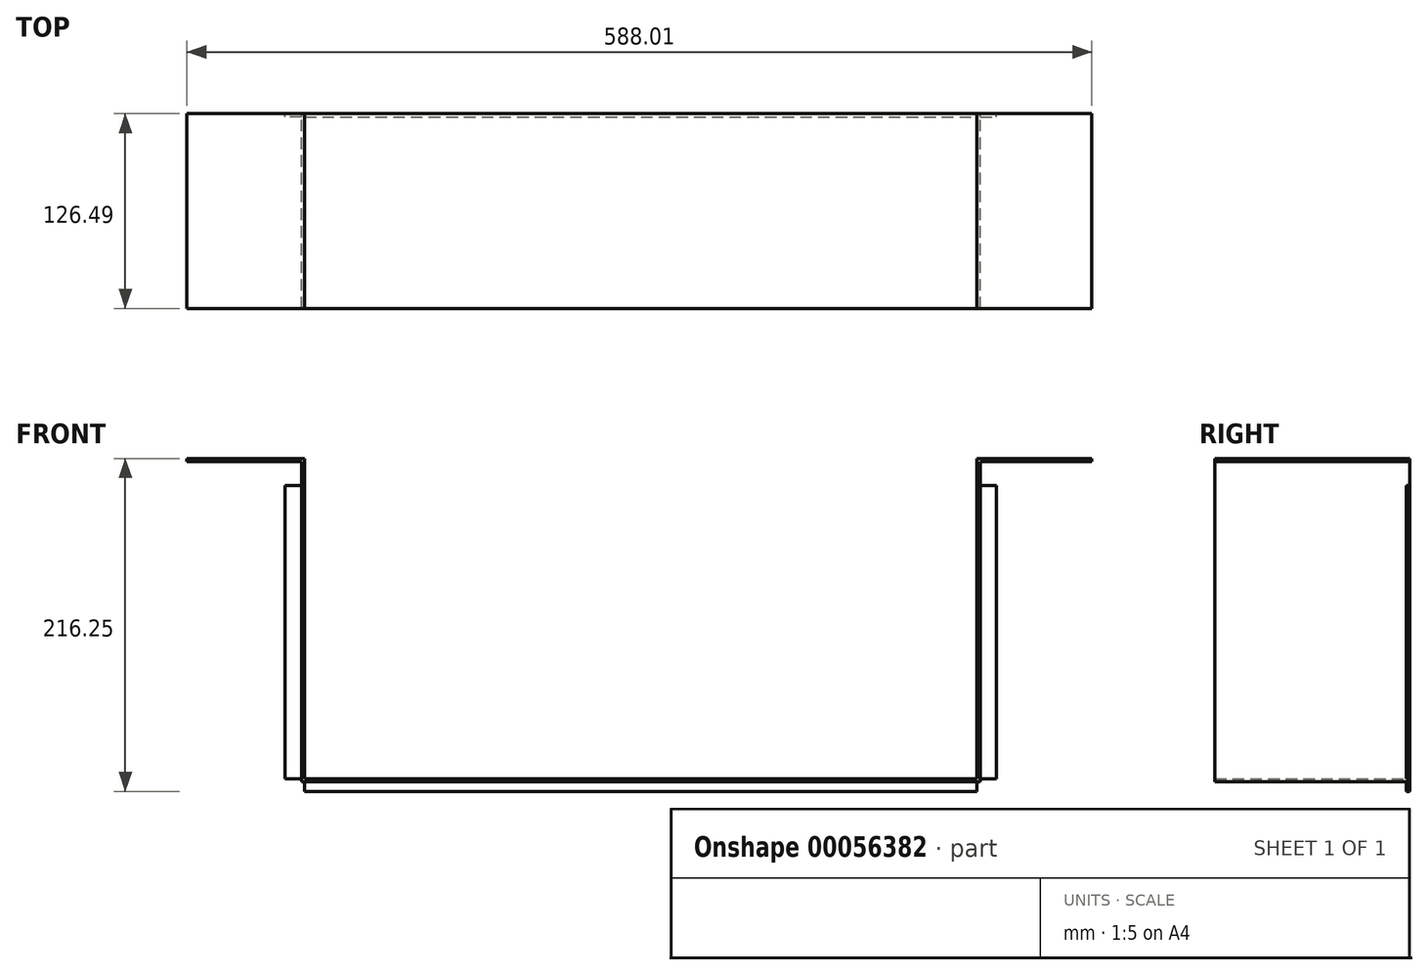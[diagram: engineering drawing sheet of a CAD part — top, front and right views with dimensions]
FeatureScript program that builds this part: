
annotation { "Feature Type Name" : "Feature", "Feature Type Description" : "" }
export const myFeature = defineFeature(function(context is Context, id is Id, definition is map)
    precondition{}
    {
        {
            var Q0;
            Q0=qCreatedBy(makeId("Front.planeOp"),FACE);
            var sketch = newSketch(context, id + "F0", { "sketchPlane" : qUnion([Q0])});
            skLineSegment(sketch, "E0", {"start": v(0, 0) * mm, "end": v(436.88, 0) * mm});
            skLineSegment(sketch, "E1", {"start": v(438.91, 0) * mm, "end": v(438.91, 206.04) * mm});
            skLineSegment(sketch, "E2", {"start": v(438.91, 206.04) * mm, "end": v(511.43, 206.04) * mm});
            skLineSegment(sketch, "E3", {"start": v(0, 0) * mm, "end": v(0, 206.04) * mm});
            skLineSegment(sketch, "E4", {"start": v(-2.03, 206.04) * mm, "end": v(-76.58, 206.04) * mm});
            skLineSegment(sketch, "E5", {"start": v(-76.58, 206.04) * mm, "end": v(-76.58, 208.08) * mm});
            skLineSegment(sketch, "E6", {"start": v(-76.58, 208.08) * mm, "end": v(-2.03, 208.08) * mm});
            skLineSegment(sketch, "E7", {"start": v(-2.03, 206.04) * mm, "end": v(-2.03, 0) * mm});
            skLineSegment(sketch, "E8", {"start": v(-2.03, -2.03) * mm, "end": v(436.88, -2.03) * mm});
            skLineSegment(sketch, "E9", {"start": v(436.88, 0) * mm, "end": v(436.88, 208.08) * mm});
            skLineSegment(sketch, "E10", {"start": v(436.88, 208.08) * mm, "end": v(511.43, 208.08) * mm});
            skLineSegment(sketch, "E11", {"start": v(511.43, 208.08) * mm, "end": v(511.43, 206.04) * mm});
            skLineSegment(sketch, "E12", {"start": v(0, -2.03) * mm, "end": v(-2.03, -2.03) * mm});
            skLineSegment(sketch, "E13", {"start": v(436.88, -2.03) * mm, "end": v(438.91, -2.03) * mm});
            skLineSegment(sketch, "E14", {"start": v(438.91, -2.03) * mm, "end": v(438.91, 0) * mm});
            skLineSegment(sketch, "E15", {"start": v(-2.03, 208.08) * mm, "end": v(0, 208.08) * mm});
            skLineSegment(sketch, "E16", {"start": v(0, 208.08) * mm, "end": v(0, 206.04) * mm});
            skLineSegment(sketch, "E17", {"start": v(-2.03, -2.03) * mm, "end": v(-2.03, 0) * mm});
            skSolve(sketch);
        }
        {
            var Q0;
            Q0 = qSketchRegion(id + "F0", true);
            extrude(context, id + "F1", {"entities" : qUnion([Q0]), "depth" : 126.5 * mm});
        }
        {
            var Q0;
            Q0=makeQuery(id+"F1.opExtrude","CAP_FACE",FACE,{"disambiguationData":[OSD([sQuery(id+"F0.wireOp",EDGE,"E0"),sQuery(id+"F0.wireOp",EDGE,"E1"),sQuery(id+"F0.wireOp",EDGE,"E2"),sQuery(id+"F0.wireOp",EDGE,"E8"),sQuery(id+"F0.wireOp",EDGE,"E9"),sQuery(id+"F0.wireOp",EDGE,"E10"),sQuery(id+"F0.wireOp",EDGE,"E11"),sQuery(id+"F0.wireOp",EDGE,"r9CPhAff-E7oF-chZl-AuHo-a7WE6WkJl8mp"),sQuery(id+"F0.wireOp",EDGE,"E13"),sQuery(id+"F0.wireOp",EDGE,"E14")])],"isStart":true});
            var sketch = newSketch(context, id + "F2", { "sketchPlane" : qUnion([Q0])});
            skLineSegment(sketch, "E18", {"start": v(-436.88, 0) * mm, "end": v(-436.88, -8.17) * mm});
            skLineSegment(sketch, "E19", {"start": v(-436.88, -8.17) * mm, "end": v(0, -8.17) * mm});
            skLineSegment(sketch, "E20", {"start": v(0, -8.17) * mm, "end": v(0, 0) * mm});
            skSolve(sketch);
        }
        {
            var Q0;
            {var subQ0=sQuery(id+"F2.wireOp",EDGE,"E19");Q0=makeQuery(id+"F2.imprint","IMPRINT",FACE,{"disambiguationData":[TD([[makeQuery(id+"F2.imprint","IMPRINT",EDGE,{"derivedFrom":subQ0}),1.0]])]});}
            extrude(context, id + "F3", {"entities" : qUnion([Q0]), "oppositeDirection" : true, "depth" : 2.03 * mm});
        }
        {
            var Q0;
            Q0=makeQuery(id+"F1.opExtrude","CAP_FACE",FACE,{"disambiguationData":[OSD([sQuery(id+"F0.wireOp",EDGE,"E0"),sQuery(id+"F0.wireOp",EDGE,"E1"),sQuery(id+"F0.wireOp",EDGE,"E2"),sQuery(id+"F0.wireOp",EDGE,"E8"),sQuery(id+"F0.wireOp",EDGE,"E9"),sQuery(id+"F0.wireOp",EDGE,"E10"),sQuery(id+"F0.wireOp",EDGE,"E11"),sQuery(id+"F0.wireOp",EDGE,"r9CPhAff-E7oF-chZl-AuHo-a7WE6WkJl8mp"),sQuery(id+"F0.wireOp",EDGE,"E13"),sQuery(id+"F0.wireOp",EDGE,"E14")])],"isStart":true});
            var sketch = newSketch(context, id + "F4", { "sketchPlane" : qUnion([Q0])});
            skLineSegment(sketch, "E21", {"start": v(-436.88, 0) * mm, "end": v(-449.58, 0) * mm});
            skLineSegment(sketch, "E22", {"start": v(-449.58, 0) * mm, "end": v(-449.58, 190.5) * mm});
            skLineSegment(sketch, "E23", {"start": v(-449.58, 190.5) * mm, "end": v(-436.88, 190.5) * mm});
            skLineSegment(sketch, "E24", {"start": v(-436.88, 190.5) * mm, "end": v(-436.88, 0) * mm});
            skLineSegment(sketch, "E25", {"start": v(0, 0) * mm, "end": v(12.7, 0) * mm});
            skLineSegment(sketch, "E26", {"start": v(12.7, 0) * mm, "end": v(12.7, 190.5) * mm});
            skLineSegment(sketch, "E27", {"start": v(12.7, 190.5) * mm, "end": v(0, 190.5) * mm});
            skLineSegment(sketch, "E28", {"start": v(0, 190.5) * mm, "end": v(0, 0) * mm});
            skSolve(sketch);
        }
        {
            var Q0;
            {var subQ0=sQuery(id+"F4.wireOp",EDGE,"E26");Q0=makeQuery(id+"F4.imprint","IMPRINT",FACE,{"disambiguationData":[TD([[makeQuery(id+"F4.imprint","IMPRINT",EDGE,{"derivedFrom":subQ0}),1.0]])]});}
            var Q1;
            {var subQ0=sQuery(id+"F4.wireOp",EDGE,"E22");Q1=makeQuery(id+"F4.imprint","IMPRINT",FACE,{"disambiguationData":[TD([[makeQuery(id+"F4.imprint","IMPRINT",EDGE,{"derivedFrom":subQ0}),-1.0]])]});}
            extrude(context, id + "F5", {"entities" : qUnion([Q0, Q1]), "operationType" : NewBodyOperationType.ADD, "oppositeDirection" : true, "depth" : 2.03 * mm});
        }
    });
